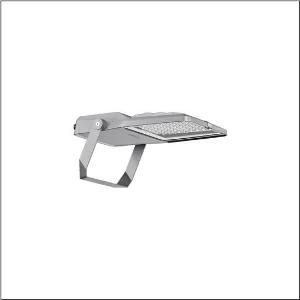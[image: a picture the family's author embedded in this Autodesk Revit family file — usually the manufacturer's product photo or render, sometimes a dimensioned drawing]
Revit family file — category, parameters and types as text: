
# Revit family: floodlight_fl_21_iq_mini___pl52_5xa7772d5d1a_a443
name_source: partatom
category: Lighting Fixtures
units: mm (PartAtom-declared; Revit-internal decimal feet)

## family parameters
Cut with Voids When Loaded = No
Host = Face
Light Source = No
Part Type = Normal
Room Calculation Point = No
Round Connector Dimension = Use Diameter
Shared = No

## types (1)
- --- (1 x LED, 16640 lm, 143 W, 4000K)
    Apparent Load = 143 VA
    CIE Flux Codes = 26 60 98 100 100
    Color Rendering = 80
    Color Temperature = 4000K
    Default Elevation = 1800 mm
    Description = Floodlight FL 21 iQ mini, floodlight, primary light control with lens, of PMMA, primary optical cover: protective disc, of toughened safety glass, transparent, light distribution: PL52, light emission: direct distribution, installation type: surface-mounted, LED, High Power LED, rated luminous flux: 16.640lm, luminous efficacy: 116lm/W, light colour: 840, colour temperature: 4000K, control: Street-Remote, Auto-Match, Temp-Guard, Night-Set, Smart-Wire, Desk-Remote (wireless, voltage-free reading and setting of iQ features in the workshop via application-optimized NFC function/RFID function), optimised constant luminous flux control (CLO 2.0), with terminal, 6-pole, mains connection: 220..240V, AC, 50/60Hz, start of lifetime: 143W, end of service life: 152W, reduction: 61W, luminaire housing, of diecast aluminium, powder-coated, Siteco® metallic grey (DB 702S), corrosivity category C5 mid according to DIN EN ISO 12944, sealing non-destructively replaceable, mounting bracket, of steel, galvanised, powder-coated, Siteco® metallic grey (DB 702S), protection rating (complete): IP66, insulation class (complete): insulation class II (safety insulation), certification: CE, ENEC, VDE, protection symbol: D, impact resistance: IK08, permissible operating ambient temperature: -40..+40°C, permissible operating ambient temperature for outdoor applications: -40..+50°C, standard: DIN EN 12944, LABS conformity tested according to VDMA 24364:2018-05, packaging unit: 1 piece

Light Distribution: PL52
    Height = 70 mm
    Lamp = 1 x LED
    Lamp Light Flux = 16640 lm
    Lamp Power = 143 W
    Lamp count = 1
    Length = 485 mm
    Luminous efficacy = 116 lm/W
    Manufacturer = Siteco
    ModVariant = No
    Model = 5XA7772D5D1A
    Number of Poles = 1
    OnlyDefault = Yes
    Power Factor = 1
    Product Name = Floodlight FL 21 iQ mini | PL52
    Product group = floodlight | pylon annexe
    ProductGroupID = 6200
    Protection Class = Protection class II
    Protection Degree = IP 66
    RLX_Detail_Level = 1
    RLX_Emergency_Light_Flux = 0 lm
    RLX_Emergency_Type = 0
    RLX_Emergency_Type_DB = No
    RlxData = <blob elided: 96537 chars, md5=7a315b8d>
    Socket = socket
    Standby Power = 0 W
    System Light Flux = 16640 lm
    System Power = 143 W
    Type Comments = factory setting: luminous flux: 100 % | dim-lin: 254 | 730 mA
    Type Image = l_1006845.jpg
    URL = http://relux.com
    VarID = @adj_113673
    Voltage = 0 V
    Weight = 0.00 kg
    Width = 337 mm

## geometry (parser evidence)
native form markers: Blend x4, Sweep x14
no freeform markers — native parametric forms only
